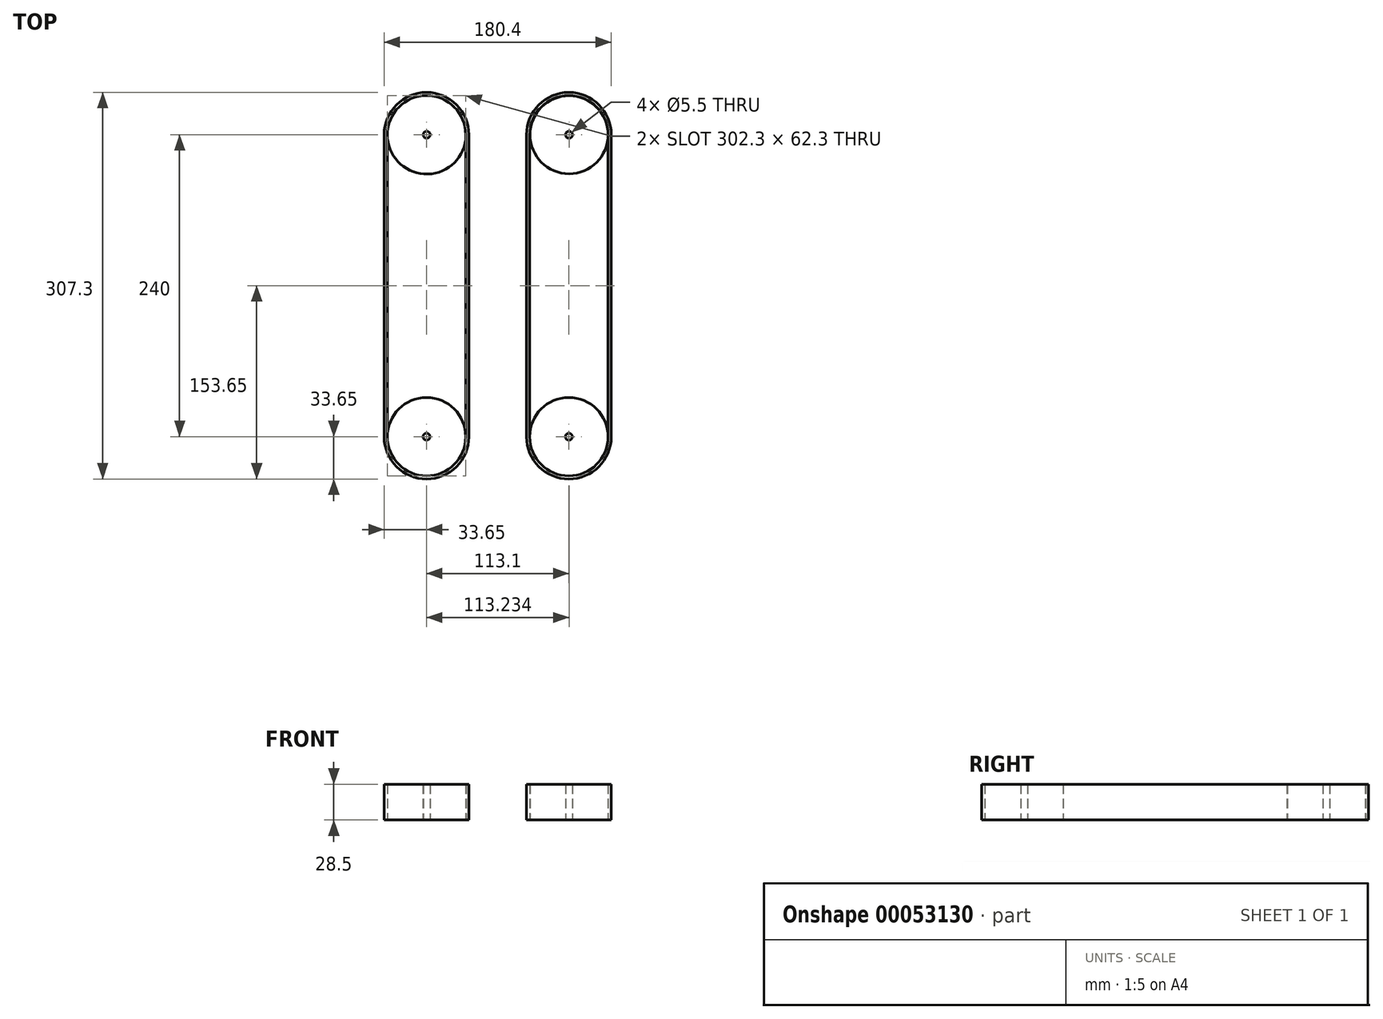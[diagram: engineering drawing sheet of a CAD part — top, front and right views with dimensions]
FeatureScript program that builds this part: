
annotation { "Feature Type Name" : "Feature", "Feature Type Description" : "" }
export const myFeature = defineFeature(function(context is Context, id is Id, definition is map)
    precondition{}
    {
        {
            var Q0;
            Q0=qCreatedBy(makeId("Top.planeOp"),FACE);
            var sketch = newSketch(context, id + "F0", { "sketchPlane" : qUnion([Q0])});
            skPoint(sketch, "E0.rect.middle", {"position": v(0, 0) * mm});
            skPoint(sketch, "E1.orphan", {"position": v(-56.42, 151.15) * mm});
            skPoint(sketch, "E2.start.orphan", {"position": v(-56.55, 0) * mm});
            skPoint(sketch, "E3", {"position": v(-56.42, 120) * mm});
            skCircle(sketch, "E4", {"center": v(-56.42, 120) * mm, "radius": 31.28 * mm});
            skPoint(sketch, "E5", {"position": v(56.68, 120) * mm});
            skCircle(sketch, "E6", {"center": v(56.68, 120) * mm, "radius": 31.02 * mm});
            skPoint(sketch, "E7", {"position": v(56.68, 151.02) * mm});
            skCircle(sketch, "E8", {"center": v(-56.55, -120) * mm, "radius": 31.15 * mm});
            skCircle(sketch, "E9", {"center": v(56.55, -120) * mm, "radius": 31.15 * mm});
            skPoint(sketch, "E10.orphan", {"position": v(-87.7, 0) * mm});
            skPoint(sketch, "E11.end.orphan", {"position": v(-25.4, 0) * mm});
            skPoint(sketch, "E12.orphan", {"position": v(-87.7, 151.15) * mm});
            skPoint(sketch, "E13.orphan", {"position": v(87.7, 151.15) * mm});
            skPoint(sketch, "E14.orphan", {"position": v(87.7, -151.15) * mm});
            skPoint(sketch, "E15.orphan", {"position": v(-87.7, -151.15) * mm});
            skPoint(sketch, "E16.orphan", {"position": v(-25.4, -120) * mm});
            skPoint(sketch, "E17.start.orphan", {"position": v(-25.13, 120) * mm});
            skPoint(sketch, "E18.end.orphan", {"position": v(25.4, -120) * mm});
            skPoint(sketch, "E18.start.orphan", {"position": v(25.67, 120) * mm});
            skCircle(sketch, "E19", {"center": v(-56.42, 120) * mm, "radius": 2.75 * mm});
            skCircle(sketch, "E20", {"center": v(56.68, 120) * mm, "radius": 2.75 * mm});
            skCircle(sketch, "E21", {"center": v(56.55, -120) * mm, "radius": 2.75 * mm});
            skCircle(sketch, "E22", {"center": v(-56.55, -120) * mm, "radius": 2.75 * mm});
            skLineSegment(sketch, "E23", {"start": v(-87.7, 120) * mm, "end": v(-87.7, 43.3) * mm});
            skLineSegment(sketch, "E24", {"start": v(-25.4, -120) * mm, "end": v(25.4, -120) * mm});
            skLineSegment(sketch, "E25", {"start": v(-87.7, 151.15) * mm, "end": v(87.7, 151.15) * mm});
            skLineSegment(sketch, "E26", {"start": v(87.7, 120) * mm, "end": v(87.7, -120) * mm});
            skLineSegment(sketch, "E27", {"start": v(87.7, -151.15) * mm, "end": v(0, -151.15) * mm});
            skPoint(sketch, "E28", {"position": v(-56.55, -151.15) * mm});
            skPoint(sketch, "E29", {"position": v(-87.7, -120) * mm});
            skPoint(sketch, "E30", {"position": v(56.55, -151.15) * mm});
            skPoint(sketch, "E31", {"position": v(87.7, -120) * mm});
            skPoint(sketch, "E32", {"position": v(-87.7, 120) * mm});
            skPoint(sketch, "E33", {"position": v(87.7, 120) * mm});
            skPoint(sketch, "E34", {"position": v(-87.7, 43.3) * mm});
            skPoint(sketch, "E35", {"position": v(-87.7, -29.86) * mm});
            skLineSegment(sketch, "E36.trimOffspring", {"start": v(-87.7, -29.86) * mm, "end": v(-87.7, -120) * mm});
            skPoint(sketch, "E37", {"position": v(-17.7, -151.15) * mm});
            skPoint(sketch, "E38", {"position": v(0, -151.15) * mm});
            skLineSegment(sketch, "E39.trimOffspring", {"start": v(-17.7, -151.15) * mm, "end": v(-87.7, -151.15) * mm});
            skLineSegment(sketch, "E40", {"start": v(-56.42, 120) * mm, "end": v(-56.55, -120) * mm});
            skSolve(sketch);
        }
        {
            var Q0;
            Q0 = qSketchRegion(id + "F0", true);
            extrude(context, id + "F1", {"entities" : qUnion([Q0]), "depth" : 28.35 * mm});
        }
        {
            var Q0;
            Q0=qCreatedBy(makeId("Top.planeOp"),FACE);
            var sketch = newSketch(context, id + "F2", { "sketchPlane" : qUnion([Q0])});
            skPoint(sketch, "E41.orphan", {"position": v(-56.55, 151.15) * mm});
            skPoint(sketch, "E42", {"position": v(-56.55, 120) * mm});
            skArc(sketch, "E43", {"start": v(-25.4, 120) * mm, "mid": v(-56.55, 151.15) * mm, "end": v(-87.7, 120) * mm});
            skPoint(sketch, "E44", {"position": v(56.55, 120) * mm});
            skArc(sketch, "E45", {"start": v(87.7, 120) * mm, "mid": v(56.55, 151.15) * mm, "end": v(25.4, 120) * mm});
            skPoint(sketch, "E46", {"position": v(56.55, 151.15) * mm});
            skArc(sketch, "E47", {"start": v(-87.7, -120) * mm, "mid": v(-56.55, -151.15) * mm, "end": v(-25.4, -120) * mm});
            skArc(sketch, "E48", {"start": v(25.4, -120) * mm, "mid": v(56.55, -151.15) * mm, "end": v(87.7, -120) * mm});
            skPoint(sketch, "E49.orphan", {"position": v(-87.7, 152.4) * mm});
            skPoint(sketch, "E50.orphan", {"position": v(87.7, 152.4) * mm});
            skPoint(sketch, "E51.orphan", {"position": v(87.7, -151.15) * mm});
            skPoint(sketch, "E52.orphan", {"position": v(-87.7, -151.15) * mm});
            skArc(sketch, "E53", {"start": v(-22.9, 120) * mm, "mid": v(-56.55, 153.65) * mm, "end": v(-90.2, 120) * mm});
            skArc(sketch, "E54", {"start": v(90.2, 120) * mm, "mid": v(56.55, 153.65) * mm, "end": v(22.9, 120) * mm});
            skArc(sketch, "E55", {"start": v(22.9, -120) * mm, "mid": v(56.55, -153.65) * mm, "end": v(90.2, -120) * mm});
            skArc(sketch, "E56", {"start": v(-90.2, -120) * mm, "mid": v(-56.55, -153.65) * mm, "end": v(-22.9, -120) * mm});
            skPoint(sketch, "E57.start.orphan", {"position": v(-22.9, 120) * mm});
            skPoint(sketch, "E58", {"position": v(-56.55, -151.15) * mm});
            skPoint(sketch, "E59", {"position": v(56.55, -151.15) * mm});
            skLineSegment(sketch, "E60", {"start": v(-56.55, 120) * mm, "end": v(-56.55, -120) * mm});
            skLineSegment(sketch, "E61", {"start": v(0, 0) * mm, "end": v(0, 120) * mm});
            skLineSegment(sketch, "E62", {"start": v(-56.55, 120) * mm, "end": v(56.55, 120) * mm});
            skPoint(sketch, "E63", {"position": v(0, 120) * mm});
            skLineSegment(sketch, "E64", {"start": v(-90.2, -120) * mm, "end": v(-90.2, 120) * mm});
            skLineSegment(sketch, "E65", {"start": v(-87.7, -120) * mm, "end": v(-87.7, 120) * mm});
            skLineSegment(sketch, "E66", {"start": v(-22.9, 120) * mm, "end": v(-22.9, -120) * mm});
            skLineSegment(sketch, "E67", {"start": v(-25.4, -120) * mm, "end": v(-25.4, 120) * mm});
            skLineSegment(sketch, "E68", {"start": v(25.4, 120) * mm, "end": v(25.4, -120) * mm});
            skLineSegment(sketch, "E69", {"start": v(90.2, -120) * mm, "end": v(90.2, 120) * mm});
            skLineSegment(sketch, "E70", {"start": v(87.7, 120) * mm, "end": v(87.7, -120) * mm});
            skLineSegment(sketch, "E71", {"start": v(22.9, -120) * mm, "end": v(22.9, 120) * mm});
            skSolve(sketch);
        }
        {
            var Q0;
            Q0 = qSketchRegion(id + "F2", true);
            extrude(context, id + "F3", {"entities" : qUnion([Q0]), "depth" : 28.5 * mm});
        }
    });
